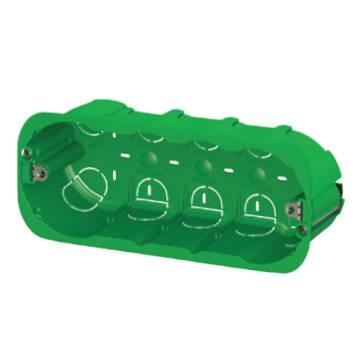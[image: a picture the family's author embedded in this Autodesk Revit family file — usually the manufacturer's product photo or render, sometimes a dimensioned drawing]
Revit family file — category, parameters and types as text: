
# Revit family: Building-ContenitoriIncasso-GEWISS-24SC-GREENWALL-SCATOLE-INCASSO_6P
name_source: partatom
category: Apparecchi elettrici
revit_build: Autodesk Revit 2016 (Build: 20161004_0715(x64)
units: mm (PartAtom-declared; Revit-internal decimal feet)

## family parameters
Condiviso = Sì
Host = Superficie
Mantenere orientamento annotazione = Sì
Numero OmniClass = 23.80.30.14.24
Punto di calcolo locali = Sì
Quota connettore circolare = Usa diametro
Taglio con vuoti quando caricato = Sì
Tipo di parte = Normale
Titolo OmniClass = Junction Boxes

## types (1)
- GW24406PM - Halogen free - 6P
    Caratteristiche = Halogen free
    Catalogo = BUILDING
    Catalogo Serie = 24SC
    Codice EAN = 8011564801936
    Codice Electrocod = 0210
    Descrizione = SCATOLA 6P.PARETI MOBILI-LEGGERE GREEN
    Descrizione: = 6 posti
    Dim. esterne BxHxP (mm) = 182x73x50
    Elementi acciaio = GEWISS - Elementi acciaio
    Glow Wire Test = 850°C
    Grado di protezione = IP40
    IDF = 7a555e11-0291-4046-b366-ca4292270978
    IDT = c923a44a-2e51-47f6-a775-de3ee192e6c0
    Immagine tipo = GW24406PM.jpg
    Installazione = Incasso
    Interasse fissaggio supporti = 100MM
    Modello = GW24406PM
    N. moduli SYSTEM = 6 posti
    Per Pareti = Cartongesso
    Predisposizione scomparti = 3
    Produttore = GEWISS S.p.A.
    Prospetto di default = 1219.2 mm  [stored 4 ft]
    Resistenza agli urti = IK07
    SEO = Scatola
    Scatola = GEWISS - scatola a incasso
    Scheda Tecnica = https://www.gewiss.com
    Temperatura di impiego = -15 +60 °C
    Termopressione con biglia = 70 °C
    Tipo Materiale = Halogen free secondo norma EN 50267-2-2
    Tipo: = Alta capienza
    URL = https://www.gewiss.com
    Versione file RFA = 19.0

note: [stored X ft] marks values corroborated as IEEE doubles in the binary element streams (Revit-internal decimal feet)

## geometry (parser evidence)
native form markers: Blend x2, Sweep x3
no freeform markers — native parametric forms only
